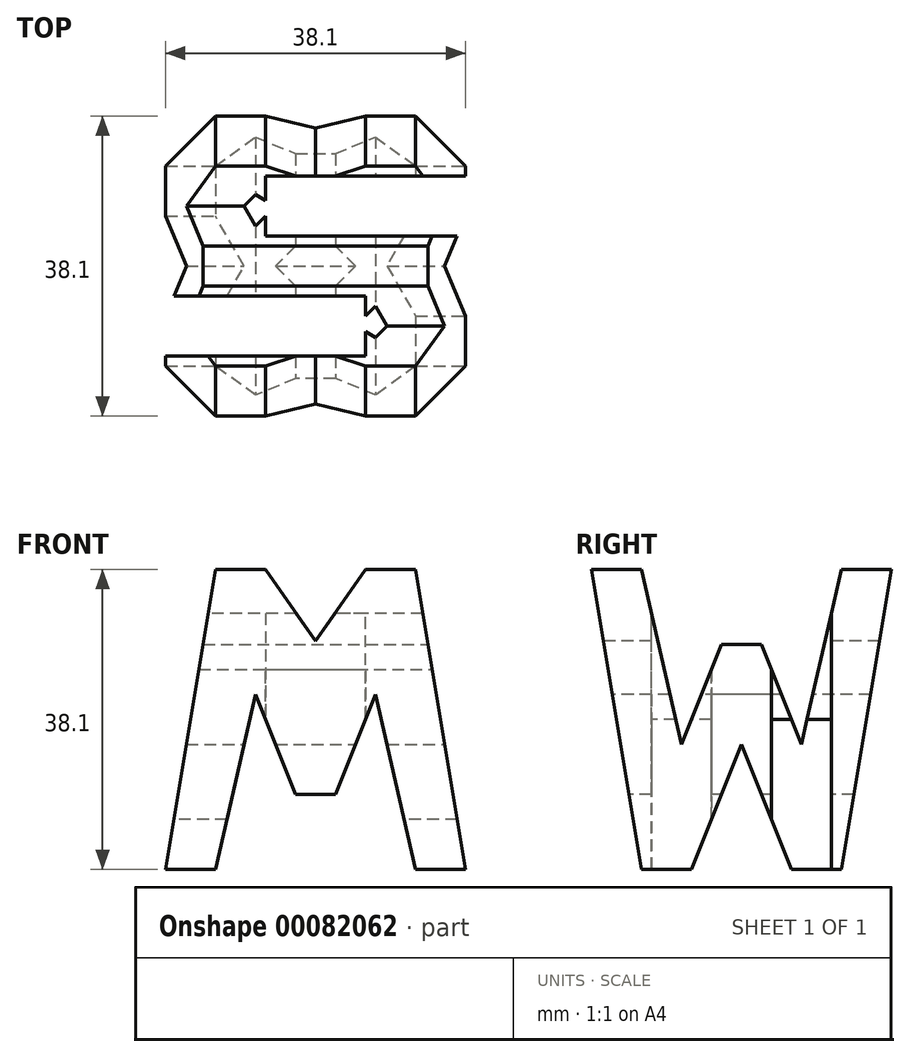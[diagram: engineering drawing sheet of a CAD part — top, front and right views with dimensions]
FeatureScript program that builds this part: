
annotation { "Feature Type Name" : "Feature", "Feature Type Description" : "" }
export const myFeature = defineFeature(function(context is Context, id is Id, definition is map)
    precondition{}
    {
        {
            var Q0;
            Q0=qCreatedBy(makeId("Front.planeOp"),FACE);
            var sketch = newSketch(context, id + "F0", { "sketchPlane" : qUnion([Q0])});
            skLineSegment(sketch, "E0", {"start": v(0, 0) * mm, "end": v(38.1, 0) * mm});
            skLineSegment(sketch, "E1", {"start": v(38.1, 0) * mm, "end": v(38.1, 38.1) * mm});
            skLineSegment(sketch, "E2", {"start": v(38.1, 38.1) * mm, "end": v(0, 38.1) * mm});
            skLineSegment(sketch, "E3", {"start": v(0, 38.1) * mm, "end": v(0, 0) * mm});
            skSolve(sketch);
        }
        {
            var Q0;
            Q0 = qSketchRegion(id + "F0", true);
            extrude(context, id + "F1", {"entities" : qUnion([Q0]), "depth" : 38.1 * mm});
        }
        {
            var Q0;
            Q0=qCreatedBy(makeId("Front.planeOp"),FACE);
            cPlane(context, id + "F2", {"entities" : qUnion([Q0]), "cplaneType" : CPlaneType.OFFSET, "offset" : 38.1 * mm, "width" : 152.4 * mm, "height" : 152.4 * mm});
        }
        {
            var Q0;
            Q0=qCreatedBy(makeId("Right.planeOp"),FACE);
            cPlane(context, id + "F3", {"entities" : qUnion([Q0]), "cplaneType" : CPlaneType.OFFSET, "offset" : 38.1 * mm, "width" : 152.4 * mm, "height" : 152.4 * mm});
        }
        {
            var Q0;
            Q0=qCreatedBy(makeId("Top.planeOp"),FACE);
            cPlane(context, id + "F4", {"entities" : qUnion([Q0]), "cplaneType" : CPlaneType.OFFSET, "offset" : 38.1 * mm, "width" : 152.4 * mm, "height" : 152.4 * mm});
        }
        {
            var Q0;
            Q0=qCreatedBy(id+"F3.planeOp",FACE);
            var sketch = newSketch(context, id + "F5", { "sketchPlane" : qUnion([Q0])});
            skLineSegment(sketch, "E4", {"start": v(0, 0) * mm, "end": v(0, 38.1) * mm});
            skLineSegment(sketch, "E5", {"start": v(0, 38.1) * mm, "end": v(-38.1, 38.1) * mm});
            skLineSegment(sketch, "E6", {"start": v(-38.1, 38.1) * mm, "end": v(-38.1, 0) * mm});
            skLineSegment(sketch, "E7", {"start": v(-38.1, 0) * mm, "end": v(0, 0) * mm});
            skLineSegment(sketch, "E8", {"start": v(-38.1, 38.1) * mm, "end": v(-31.75, 0) * mm});
            skLineSegment(sketch, "E9", {"start": v(-31.75, 0) * mm, "end": v(-25.4, 0) * mm});
            skLineSegment(sketch, "E10", {"start": v(-25.4, 0) * mm, "end": v(-19.05, 15.88) * mm});
            skLineSegment(sketch, "E11", {"start": v(-19.05, 15.88) * mm, "end": v(-12.7, 0) * mm});
            skLineSegment(sketch, "E12", {"start": v(-12.7, 0) * mm, "end": v(-6.35, 0) * mm});
            skLineSegment(sketch, "E13", {"start": v(-6.35, 0) * mm, "end": v(0, 38.1) * mm});
            skLineSegment(sketch, "E14", {"start": v(-6.35, 38.1) * mm, "end": v(-11.43, 15.87) * mm});
            skLineSegment(sketch, "E15", {"start": v(-11.43, 15.87) * mm, "end": v(-16.51, 28.58) * mm});
            skLineSegment(sketch, "E16", {"start": v(-16.51, 28.58) * mm, "end": v(-21.6, 28.58) * mm});
            skLineSegment(sketch, "E17", {"start": v(-21.6, 28.58) * mm, "end": v(-26.67, 15.88) * mm});
            skLineSegment(sketch, "E18", {"start": v(-26.67, 15.88) * mm, "end": v(-31.75, 38.1) * mm});
            skLineSegment(sketch, "E19", {"start": v(-31.75, 38.1) * mm, "end": v(-38.1, 38.1) * mm});
            skSolve(sketch);
        }
        {
            var Q0;
            {var subQ0=sQuery(id+"F5.wireOp",EDGE,"E14");Q0=makeQuery(id+"F5.imprint","IMPRINT",FACE,{"disambiguationData":[TD([[makeQuery(id+"F5.imprint","IMPRINT",EDGE,{"derivedFrom":subQ0}),-1.0]])]});}
            var Q1;
            {var subQ0=sQuery(id+"F5.wireOp",EDGE,"E10");Q1=makeQuery(id+"F5.imprint","IMPRINT",FACE,{"disambiguationData":[TD([[makeQuery(id+"F5.imprint","IMPRINT",EDGE,{"derivedFrom":subQ0}),-1.0]])]});}
            var Q2;
            {var subQ0=sQuery(id+"F5.wireOp",EDGE,"E4");Q2=makeQuery(id+"F5.imprint","IMPRINT",FACE,{"disambiguationData":[TD([[makeQuery(id+"F5.imprint","IMPRINT",EDGE,{"derivedFrom":subQ0}),1.0]])]});}
            var Q3;
            {var subQ0=sQuery(id+"F5.wireOp",EDGE,"E6");Q3=makeQuery(id+"F5.imprint","IMPRINT",FACE,{"disambiguationData":[TD([[makeQuery(id+"F5.imprint","IMPRINT",EDGE,{"derivedFrom":subQ0}),1.0]])]});}
            extrude(context, id + "F6", {"entities" : qUnion([Q0, Q1, Q2, Q3]), "operationType" : NewBodyOperationType.REMOVE, "oppositeDirection" : true, "depth" : 38.1 * mm});
        }
        {
            var Q0;
            Q0=qCreatedBy(id+"F2.planeOp",FACE);
            var sketch = newSketch(context, id + "F7", { "sketchPlane" : qUnion([Q0])});
            skLineSegment(sketch, "E20.bottom", {"start": v(0, 0) * mm, "end": v(38.1, 0) * mm});
            skLineSegment(sketch, "E20.top", {"start": v(0, 38.1) * mm, "end": v(38.1, 38.1) * mm});
            skLineSegment(sketch, "E20.left", {"start": v(0, 0) * mm, "end": v(0, 38.1) * mm});
            skLineSegment(sketch, "E20.right", {"start": v(38.1, 0) * mm, "end": v(38.1, 38.1) * mm});
            skLineSegment(sketch, "E21", {"start": v(0, 0) * mm, "end": v(6.35, 38.1) * mm});
            skLineSegment(sketch, "E22", {"start": v(6.35, 38.1) * mm, "end": v(12.7, 38.1) * mm});
            skLineSegment(sketch, "E23", {"start": v(12.7, 38.1) * mm, "end": v(19.05, 29.03) * mm});
            skLineSegment(sketch, "E24", {"start": v(19.05, 29.03) * mm, "end": v(25.4, 38.1) * mm});
            skLineSegment(sketch, "E25", {"start": v(25.4, 38.1) * mm, "end": v(31.75, 38.1) * mm});
            skLineSegment(sketch, "E26", {"start": v(31.75, 38.1) * mm, "end": v(38.1, 0) * mm});
            skLineSegment(sketch, "E27", {"start": v(31.75, 0) * mm, "end": v(26.67, 22.23) * mm});
            skLineSegment(sketch, "E28", {"start": v(26.67, 22.23) * mm, "end": v(21.59, 9.53) * mm});
            skLineSegment(sketch, "E29", {"start": v(21.59, 9.53) * mm, "end": v(16.51, 9.53) * mm});
            skLineSegment(sketch, "E30", {"start": v(16.51, 9.53) * mm, "end": v(11.43, 22.23) * mm});
            skLineSegment(sketch, "E31", {"start": v(11.43, 22.23) * mm, "end": v(6.35, 0) * mm});
            skLineSegment(sketch, "E32", {"start": v(6.35, 0) * mm, "end": v(0, 0) * mm});
            skSolve(sketch);
        }
        {
            var Q0;
            {var subQ0=sQuery(id+"F7.wireOp",EDGE,"E20.left");Q0=makeQuery(id+"F7.imprint","IMPRINT",FACE,{"disambiguationData":[TD([[makeQuery(id+"F7.imprint","IMPRINT",EDGE,{"derivedFrom":subQ0}),-1.0]])]});}
            var Q1;
            {var subQ0=sQuery(id+"F7.wireOp",EDGE,"E23");Q1=makeQuery(id+"F7.imprint","IMPRINT",FACE,{"disambiguationData":[TD([[makeQuery(id+"F7.imprint","IMPRINT",EDGE,{"derivedFrom":subQ0}),1.0]])]});}
            var Q2;
            {var subQ0=sQuery(id+"F7.wireOp",EDGE,"E20.right");Q2=makeQuery(id+"F7.imprint","IMPRINT",FACE,{"disambiguationData":[TD([[makeQuery(id+"F7.imprint","IMPRINT",EDGE,{"derivedFrom":subQ0}),1.0]])]});}
            var Q3;
            {var subQ2=sQuery(id+"F7.wireOp",EDGE,"E27");Q3=makeQuery(id+"F7.imprint","IMPRINT",FACE,{"disambiguationData":[TD([[makeQuery(id+"F7.imprint","IMPRINT",EDGE,{"derivedFrom":subQ2}),1.0]])]});}
            extrude(context, id + "F8", {"entities" : qUnion([Q0, Q1, Q2, Q3]), "operationType" : NewBodyOperationType.REMOVE, "oppositeDirection" : true, "depth" : 38.1 * mm});
        }
        {
            var Q0;
            Q0=qCreatedBy(id+"F4.planeOp",FACE);
            var sketch = newSketch(context, id + "F9", { "sketchPlane" : qUnion([Q0])});
            skLineSegment(sketch, "E33", {"start": v(0, 0) * mm, "end": v(0, -38.1) * mm});
            skLineSegment(sketch, "E34", {"start": v(0, -38.1) * mm, "end": v(38.1, -38.1) * mm});
            skLineSegment(sketch, "E35", {"start": v(38.1, -38.1) * mm, "end": v(38.1, 0) * mm});
            skLineSegment(sketch, "E36", {"start": v(38.1, 0) * mm, "end": v(0, 0) * mm});
            skLineSegment(sketch, "E37", {"start": v(38.1, -7.62) * mm, "end": v(12.7, -7.62) * mm});
            skLineSegment(sketch, "E38", {"start": v(12.7, -7.62) * mm, "end": v(12.7, -15.24) * mm});
            skLineSegment(sketch, "E39", {"start": v(12.7, -15.24) * mm, "end": v(38.1, -15.24) * mm});
            skLineSegment(sketch, "E40", {"start": v(38.1, -15.24) * mm, "end": v(38.1, -7.62) * mm});
            skLineSegment(sketch, "E41", {"start": v(0, -22.86) * mm, "end": v(25.4, -22.86) * mm});
            skLineSegment(sketch, "E42", {"start": v(25.4, -22.86) * mm, "end": v(25.4, -30.48) * mm});
            skLineSegment(sketch, "E43", {"start": v(25.4, -30.48) * mm, "end": v(0, -30.48) * mm});
            skLineSegment(sketch, "E44", {"start": v(0, -30.48) * mm, "end": v(0, -22.86) * mm});
            skSolve(sketch);
        }
        {
            var Q0;
            Q0=makeQuery(id+"F9.imprint","IMPRINT",FACE,{"disambiguationData":[TD([[makeQuery(id+"F9.imprint","IMPRINT",EDGE,{"derivedFrom":sQuery(id+"F9.wireOp",EDGE,"E37")}),1.0]])]});
            var Q1;
            Q1=makeQuery(id+"F9.imprint","IMPRINT",FACE,{"disambiguationData":[TD([[makeQuery(id+"F9.imprint","IMPRINT",EDGE,{"derivedFrom":sQuery(id+"F9.wireOp",EDGE,"E41")}),-1.0]])]});
            extrude(context, id + "F10", {"entities" : qUnion([Q0, Q1]), "operationType" : NewBodyOperationType.REMOVE, "oppositeDirection" : true, "depth" : 38.1 * mm});
        }
    });
